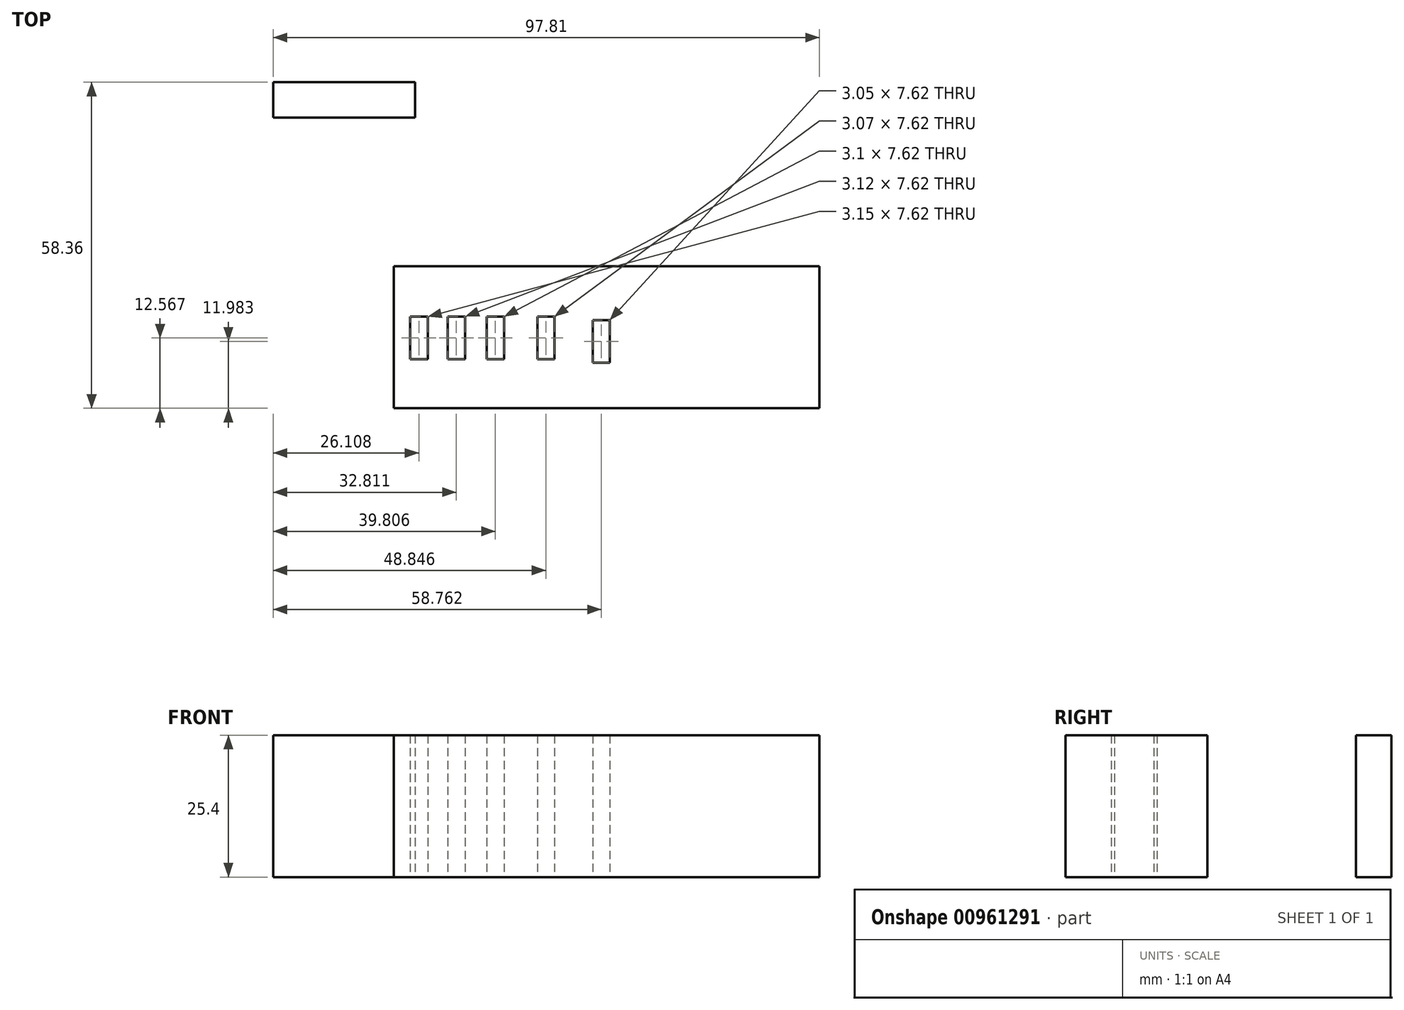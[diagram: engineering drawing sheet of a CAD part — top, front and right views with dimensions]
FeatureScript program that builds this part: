
annotation { "Feature Type Name" : "Feature", "Feature Type Description" : "" }
export const myFeature = defineFeature(function(context is Context, id is Id, definition is map)
    precondition{}
    {
        {
            var Q0;
            Q0=qCreatedBy(makeId("Top.planeOp"),FACE);
            var sketch = newSketch(context, id + "F0", { "sketchPlane" : qUnion([Q0])});
            skLineSegment(sketch, "E0", {"start": v(-72.86, 25.22) * mm, "end": v(-72.86, 18.87) * mm});
            skLineSegment(sketch, "E1", {"start": v(-72.86, 25.22) * mm, "end": v(-47.46, 25.22) * mm});
            skLineSegment(sketch, "E2", {"start": v(-47.46, 25.22) * mm, "end": v(-47.46, 18.87) * mm});
            skLineSegment(sketch, "E3", {"start": v(-72.86, 18.87) * mm, "end": v(-47.46, 18.87) * mm});
            skLineSegment(sketch, "E4", {"start": v(-51.25, -7.74) * mm, "end": v(-51.25, -33.14) * mm});
            skLineSegment(sketch, "E5", {"start": v(-51.25, -33.14) * mm, "end": v(24.95, -33.14) * mm});
            skLineSegment(sketch, "E6", {"start": v(24.95, -33.14) * mm, "end": v(24.95, -7.74) * mm});
            skLineSegment(sketch, "E7", {"start": v(-51.25, -7.74) * mm, "end": v(24.95, -7.74) * mm});
            skLineSegment(sketch, "E8", {"start": v(-48.33, -16.76) * mm, "end": v(-48.33, -24.38) * mm});
            skLineSegment(sketch, "E9", {"start": v(-48.33, -16.76) * mm, "end": v(-45.18, -16.76) * mm});
            skLineSegment(sketch, "E10", {"start": v(-45.18, -16.76) * mm, "end": v(-45.18, -24.38) * mm});
            skLineSegment(sketch, "E11", {"start": v(-48.33, -24.38) * mm, "end": v(-45.18, -24.38) * mm});
            skLineSegment(sketch, "E12", {"start": v(-41.61, -16.76) * mm, "end": v(-41.61, -24.38) * mm});
            skLineSegment(sketch, "E13", {"start": v(-41.61, -24.38) * mm, "end": v(-38.49, -24.38) * mm});
            skLineSegment(sketch, "E14", {"start": v(-41.61, -16.76) * mm, "end": v(-38.49, -16.76) * mm});
            skLineSegment(sketch, "E15", {"start": v(-38.49, -16.76) * mm, "end": v(-38.49, -24.38) * mm});
            skLineSegment(sketch, "E16", {"start": v(-34.6, -16.76) * mm, "end": v(-34.6, -24.38) * mm});
            skLineSegment(sketch, "E17", {"start": v(-34.6, -24.38) * mm, "end": v(-31.5, -24.38) * mm});
            skLineSegment(sketch, "E18", {"start": v(-31.5, -24.38) * mm, "end": v(-31.5, -16.76) * mm});
            skLineSegment(sketch, "E19", {"start": v(-34.6, -16.76) * mm, "end": v(-31.5, -16.76) * mm});
            skLineSegment(sketch, "E20", {"start": v(-25.55, -16.76) * mm, "end": v(-25.55, -24.38) * mm});
            skLineSegment(sketch, "E21", {"start": v(-25.55, -16.76) * mm, "end": v(-22.48, -16.76) * mm});
            skLineSegment(sketch, "E22", {"start": v(-22.48, -16.76) * mm, "end": v(-22.48, -24.38) * mm});
            skLineSegment(sketch, "E23", {"start": v(-25.55, -24.38) * mm, "end": v(-22.48, -24.38) * mm});
            skLineSegment(sketch, "E24", {"start": v(-15.62, -17.35) * mm, "end": v(-15.62, -24.97) * mm});
            skLineSegment(sketch, "E25", {"start": v(-15.62, -24.97) * mm, "end": v(-12.57, -24.97) * mm});
            skLineSegment(sketch, "E26", {"start": v(-12.57, -24.97) * mm, "end": v(-12.57, -17.35) * mm});
            skLineSegment(sketch, "E27", {"start": v(-15.62, -17.35) * mm, "end": v(-12.57, -17.35) * mm});
            skSolve(sketch);
        }
        {
            var Q0;
            Q0 = qSketchRegion(id + "F0", true);
            extrude(context, id + "F1", {"entities" : qUnion([Q0]), "depth" : 25.4 * mm, "offsetDistance" : 25.4 * mm});
        }
    });
